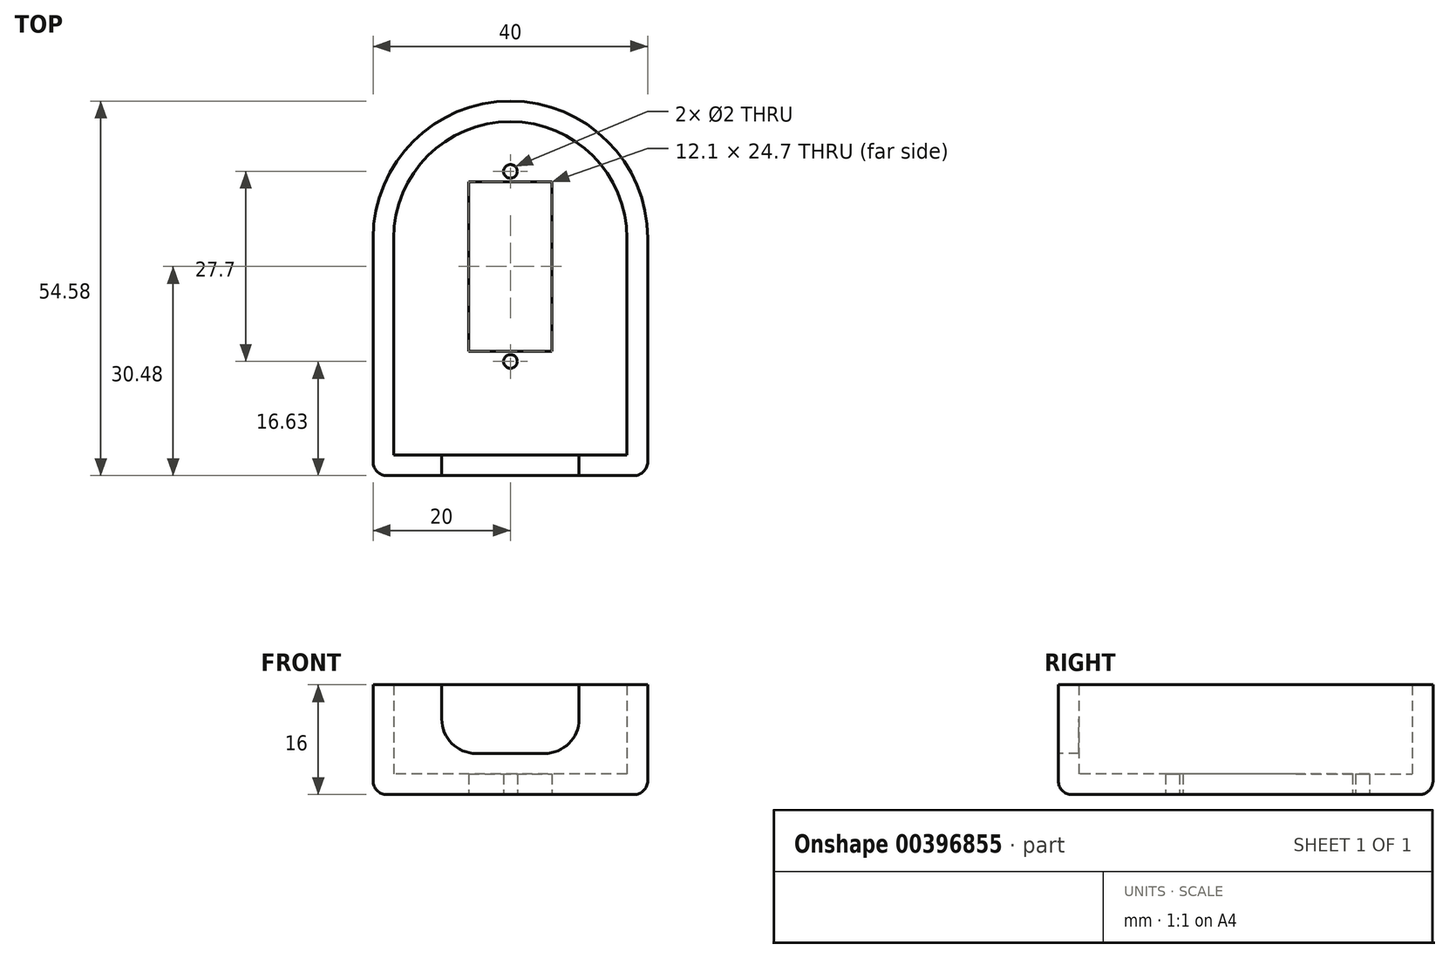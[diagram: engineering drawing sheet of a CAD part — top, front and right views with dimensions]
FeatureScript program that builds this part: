
annotation { "Feature Type Name" : "Feature", "Feature Type Description" : "" }
export const myFeature = defineFeature(function(context is Context, id is Id, definition is map)
    precondition{}
    {
        {
            var Q0;
            Q0=qCreatedBy(makeId("Top.planeOp"),FACE);
            var sketch = newSketch(context, id + "F0", { "sketchPlane" : qUnion([Q0])});
            skLineSegment(sketch, "E0.bottom", {"start": v(0, 22.7) * mm, "end": v(12.1, 22.7) * mm});
            skLineSegment(sketch, "E0.top", {"start": v(0, 0) * mm, "end": v(12.1, 0) * mm});
            skLineSegment(sketch, "E0.left", {"start": v(0, 22.7) * mm, "end": v(0, 0) * mm});
            skLineSegment(sketch, "E0.right", {"start": v(12.1, 22.7) * mm, "end": v(12.1, 0) * mm});
            skLineSegment(sketch, "E1.bottom", {"start": v(-3, 27.5) * mm, "end": v(15.1, 27.5) * mm});
            skLineSegment(sketch, "E1.top", {"start": v(-3, -4.8) * mm, "end": v(15.1, -4.8) * mm});
            skLineSegment(sketch, "E1.left", {"start": v(-3, 27.5) * mm, "end": v(-3, -4.8) * mm});
            skLineSegment(sketch, "E1.right", {"start": v(15.1, 27.5) * mm, "end": v(15.1, -4.8) * mm});
            skLineSegment(sketch, "E2", {"start": v(0, 11.35) * mm, "end": v(-3, 11.35) * mm});
            skPoint(sketch, "E2.startSnap0", {"position": v(0, 11.35) * mm});
            skCircle(sketch, "E3", {"center": v(6.05, -2.5) * mm, "radius": 1 * mm});
            skPoint(sketch, "E3.centerSnap0", {"position": v(6.05, 0) * mm});
            skCircle(sketch, "E4", {"center": v(6.05, 25.2) * mm, "radius": 1 * mm});
            skPoint(sketch, "E4.centerSnap0", {"position": v(6.05, 22.7) * mm});
            skLineSegment(sketch, "E5.top", {"start": v(-13.95, -19.13) * mm, "end": v(26.05, -19.13) * mm});
            skLineSegment(sketch, "E5.left", {"start": v(-13.95, 15.45) * mm, "end": v(-13.95, -19.13) * mm});
            skLineSegment(sketch, "E5.right", {"start": v(26.05, 15.45) * mm, "end": v(26.05, -19.13) * mm});
            skLineSegment(sketch, "E6", {"start": v(6.05, -19.13) * mm, "end": v(6.05, 0) * mm});
            skCircle(sketch, "E7", {"center": v(6.05, 15.45) * mm, "radius": 20 * mm});
            skCircle(sketch, "E8", {"center": v(6.05, 15.45) * mm, "radius": 17 * mm});
            skLineSegment(sketch, "E9", {"start": v(-10.95, 15.45) * mm, "end": v(-10.95, -16.13) * mm});
            skLineSegment(sketch, "E10", {"start": v(-10.95, -16.13) * mm, "end": v(23.05, -16.13) * mm});
            skLineSegment(sketch, "E11", {"start": v(23.05, -16.13) * mm, "end": v(23.05, 15.45) * mm});
            skLineSegment(sketch, "E12.bottom", {"start": v(0, -1) * mm, "end": v(12.1, -1) * mm});
            skLineSegment(sketch, "E12.top", {"start": v(0, 23.7) * mm, "end": v(12.1, 23.7) * mm});
            skLineSegment(sketch, "E12.left", {"start": v(0, -1) * mm, "end": v(0, 23.7) * mm});
            skLineSegment(sketch, "E12.right", {"start": v(12.1, -1) * mm, "end": v(12.1, 23.7) * mm});
            skSolve(sketch);
        }
        {
            var Q0;
            Q0 = qSketchRegion(id + "F0", true);
            var Q1;
            {var subQ3=sQuery(id+"F0.wireOp",EDGE,"E2");Q1=makeQuery(id+"F0.imprint","IMPRINT",FACE,{"disambiguationData":[TD([[makeQuery(id+"F0.imprint","IMPRINT",EDGE,{"derivedFrom":subQ3}),1.0]])]});}
            var Q2;
            {var subQ0=sQuery(id+"F0.wireOp",EDGE,"E10");var subQ1=sQuery(id+"F0.wireOp",EDGE,"E6");var subQ2=makeQuery(id+"F0.imprint","INTERSECT",VERTEX,{"derivedFrom":[subQ1,subQ0]});Q2=makeQuery(id+"F0.imprint","IMPRINT",FACE,{"disambiguationData":[TD([[makeQuery(id+"F0.imprint","IMPRINT",EDGE,{"disambiguationData":[TD([[subQ2,-1.0]])],"derivedFrom":subQ1}),1.0]])]});}
            var Q3;
            {var subQ0=sQuery(id+"F0.wireOp",EDGE,"E10");var subQ1=sQuery(id+"F0.wireOp",EDGE,"E6");var subQ2=makeQuery(id+"F0.imprint","INTERSECT",VERTEX,{"derivedFrom":[subQ1,subQ0]});Q3=makeQuery(id+"F0.imprint","IMPRINT",FACE,{"disambiguationData":[TD([[makeQuery(id+"F0.imprint","IMPRINT",EDGE,{"disambiguationData":[TD([[subQ2,-1.0]])],"derivedFrom":subQ1}),-1.0]])]});}
            var Q4;
            {var subQ1=sQuery(id+"F0.wireOp",EDGE,"E1.bottom");Q4=makeQuery(id+"F0.imprint","IMPRINT",FACE,{"disambiguationData":[TD([[makeQuery(id+"F0.imprint","IMPRINT",EDGE,{"derivedFrom":subQ1}),1.0]])]});}
            var Q5;
            {var subQ0=sQuery(id+"F0.wireOp",EDGE,"E8");var subQ1=sQuery(id+"F0.wireOp",EDGE,"E1.right");var subQ2=makeQuery(id+"F0.imprint","INTERSECT",VERTEX,{"derivedFrom":[subQ1,subQ0]});Q5=makeQuery(id+"F0.imprint","IMPRINT",FACE,{"disambiguationData":[TD([[makeQuery(id+"F0.imprint","IMPRINT",EDGE,{"disambiguationData":[TD([[subQ2,-1.0]])],"derivedFrom":subQ1}),1.0]])]});}
            var Q6;
            {var subQ0=sQuery(id+"F0.wireOp",EDGE,"E8");var subQ1=sQuery(id+"F0.wireOp",EDGE,"E1.left");var subQ2=makeQuery(id+"F0.imprint","INTERSECT",VERTEX,{"derivedFrom":[subQ1,subQ0]});Q6=makeQuery(id+"F0.imprint","IMPRINT",FACE,{"disambiguationData":[TD([[makeQuery(id+"F0.imprint","IMPRINT",EDGE,{"disambiguationData":[TD([[subQ2,-1.0]])],"derivedFrom":subQ1}),-1.0]])]});}
            var Q7;
            {var subQ5=sQuery(id+"F0.wireOp",EDGE,"E8");var subQ7=sQuery(id+"F0.wireOp",EDGE,"E1.left");var subQ9=makeQuery(id+"F0.imprint","INTERSECT",VERTEX,{"derivedFrom":[subQ7,subQ5]});Q7=makeQuery(id+"F0.imprint","IMPRINT",FACE,{"disambiguationData":[TD([[makeQuery(id+"F0.imprint","IMPRINT",EDGE,{"disambiguationData":[TD([[subQ9,-1.0]])],"derivedFrom":subQ7}),1.0]])]});}
            var Q8;
            {var subQ0=sQuery(id+"F0.wireOp",EDGE,"E1.left");var subQ1=sQuery(id+"F0.wireOp",EDGE,"E1.top");var subQ2=makeQuery(id+"F0.imprint","INTERSECT",VERTEX,{"derivedFrom":[subQ1,subQ0]});Q8=makeQuery(id+"F0.imprint","IMPRINT",FACE,{"disambiguationData":[TD([[makeQuery(id+"F0.imprint","IMPRINT",EDGE,{"disambiguationData":[TD([[subQ2,-1.0]])],"derivedFrom":subQ1}),1.0]])]});}
            var Q9;
            {var subQ0=sQuery(id+"F0.wireOp",EDGE,"E1.right");var subQ1=sQuery(id+"F0.wireOp",EDGE,"E1.top");var subQ2=makeQuery(id+"F0.imprint","INTERSECT",VERTEX,{"derivedFrom":[subQ1,subQ0]});Q9=makeQuery(id+"F0.imprint","IMPRINT",FACE,{"disambiguationData":[TD([[makeQuery(id+"F0.imprint","IMPRINT",EDGE,{"disambiguationData":[TD([[subQ2,1.0]])],"derivedFrom":subQ1}),1.0]])]});}
            var Q10;
            {var subQ1=sQuery(id+"F0.wireOp",EDGE,"E1.right");var subQ5=sQuery(id+"F0.wireOp",EDGE,"E8");var subQ9=makeQuery(id+"F0.imprint","INTERSECT",VERTEX,{"derivedFrom":[subQ1,subQ5]});Q10=makeQuery(id+"F0.imprint","IMPRINT",FACE,{"disambiguationData":[TD([[makeQuery(id+"F0.imprint","IMPRINT",EDGE,{"disambiguationData":[TD([[subQ9,-1.0]])],"derivedFrom":subQ1}),-1.0]])]});}
            var Q11;
            {var subQ0=sQuery(id+"F0.wireOp",EDGE,"E6");var subQ1=sQuery(id+"F0.wireOp",EDGE,"E3");var subQ2=makeQuery(id+"F0.imprint","INTERSECT",VERTEX,{"disambiguationData":[OD(0.0)],"derivedFrom":[subQ1,subQ0]});Q11=makeQuery(id+"F0.imprint","IMPRINT",FACE,{"disambiguationData":[TD([[makeQuery(id+"F0.imprint","IMPRINT",EDGE,{"disambiguationData":[TD([[subQ2,1.0]])],"derivedFrom":subQ1}),-1.0]])]});}
            var Q12;
            {var subQ0=sQuery(id+"F0.wireOp",EDGE,"E6");var subQ1=sQuery(id+"F0.wireOp",EDGE,"E3");var subQ2=makeQuery(id+"F0.imprint","INTERSECT",VERTEX,{"disambiguationData":[OD(0.0)],"derivedFrom":[subQ1,subQ0]});Q12=makeQuery(id+"F0.imprint","IMPRINT",FACE,{"disambiguationData":[TD([[makeQuery(id+"F0.imprint","IMPRINT",EDGE,{"disambiguationData":[TD([[subQ2,-1.0]])],"derivedFrom":subQ1}),-1.0]])]});}
            var Q13;
            {var subQ11=sQuery(id+"F0.wireOp",EDGE,"E1.bottom");Q13=makeQuery(id+"F0.imprint","IMPRINT",FACE,{"disambiguationData":[TD([[makeQuery(id+"F0.imprint","IMPRINT",EDGE,{"derivedFrom":subQ11}),-1.0]])]});}
            extrude(context, id + "F1", {"entities" : qUnion([Q0, Q1, Q2, Q3, Q4, Q5, Q6, Q7, Q8, Q9, Q10, Q11, Q12, Q13]), "depth" : 3 * mm});
        }
        {
            var Q0;
            {var subQ1=sQuery(id+"F0.wireOp",EDGE,"E5.left");Q0=makeQuery(id+"F0.imprint","IMPRINT",FACE,{"disambiguationData":[TD([[makeQuery(id+"F0.imprint","IMPRINT",EDGE,{"derivedFrom":subQ1}),1.0]])]});}
            var Q1;
            {var subQ1=sQuery(id+"F0.wireOp",EDGE,"E5.right");Q1=makeQuery(id+"F0.imprint","IMPRINT",FACE,{"disambiguationData":[TD([[makeQuery(id+"F0.imprint","IMPRINT",EDGE,{"derivedFrom":subQ1}),-1.0]])]});}
            var Q2;
            {var subQ0=sQuery(id+"F0.wireOp",EDGE,"E7");var subQ4=makeQuery(id+"F0.imprint","INTERSECT",VERTEX,{"derivedFrom":[sQuery(id+"F0.wireOp",EDGE,"E5.left"),subQ0]});Q2=makeQuery(id+"F0.imprint","IMPRINT",FACE,{"disambiguationData":[TD([[makeQuery(id+"F0.imprint","IMPRINT",EDGE,{"disambiguationData":[TD([[subQ4,1.0]])],"derivedFrom":subQ0}),1.0]])]});}
            extrude(context, id + "F2", {"entities" : qUnion([Q0, Q1, Q2]), "operationType" : NewBodyOperationType.ADD, "depth" : 16 * mm});
        }
        {
            var Q0;
            Q0=makeQuery(id+"F2.opExtrude","CAP_EDGE",EDGE,{"disambiguationData":[OSD([sQuery(id+"FoOm9mcpyAAcKK5_1.wireOp",EDGE,"GcfQukfY-8nN6-G3zW-65xT-WTSIB9kCBruh.right")])],"isStart":true});
            var Q1;
            Q1=makeQuery(id+"F2.opExtrude","CAP_EDGE",EDGE,{"disambiguationData":[OSD([sQuery(id+"FoOm9mcpyAAcKK5_1.wireOp",EDGE,"54IPlG1U-AUWy-TRX5-auCB-k9ajS3RtIQhU.right")])],"isStart":true});
            var Q2;
            Q2=makeQuery(id+"F1.opExtrude","CAP_EDGE",EDGE,{"disambiguationData":[OSD([sQuery(id+"F0.wireOp",EDGE,"E5.right")])],"isStart":true});
            var Q3;
            Q3=makeQuery(id+"F1.opExtrude","CAP_EDGE",EDGE,{"disambiguationData":[OSD([sQuery(id+"F0.wireOp",EDGE,"E5.left")])],"isStart":true});
            var Q4;
            Q4=makeQuery(id+"F1.opExtrude","CAP_EDGE",EDGE,{"disambiguationData":[OSD([sQuery(id+"F0.wireOp",EDGE,"E5.top")])],"isStart":true});
            var Q5;
            {var subQ0=sQuery(id+"F0.wireOp",EDGE,"E5.right");var subQ1=sQuery(id+"F0.wireOp",EDGE,"E5.top");Q5=makeQuery(id+"F2.boolean.opBoolean","MERGE",EDGE,{"derivedFrom":[makeQuery(id+"F1.opExtrude","SWEPT_EDGE",EDGE,{"disambiguationData":[OSD([subQ1,subQ0])]}),makeQuery(id+"F2.opExtrude","SWEPT_EDGE",EDGE,{"disambiguationData":[OSD([subQ1,subQ0])]})]});}
            var Q6;
            {var subQ0=sQuery(id+"F0.wireOp",EDGE,"E5.left");var subQ1=sQuery(id+"F0.wireOp",EDGE,"E5.top");Q6=makeQuery(id+"F2.boolean.opBoolean","MERGE",EDGE,{"derivedFrom":[makeQuery(id+"F1.opExtrude","SWEPT_EDGE",EDGE,{"disambiguationData":[OSD([subQ1,subQ0])]}),makeQuery(id+"F2.opExtrude","SWEPT_EDGE",EDGE,{"disambiguationData":[OSD([subQ1,subQ0])]})]});}
            fillet(context, id + "F3", {"entities" : qUnion([Q0, Q1, Q2, Q3, Q4, Q5, Q6]), "radius" : 2 * mm, "tangentPropagation" : true, "allowEdgeOverflow" : false});
        }
        {
            var Q0;
            {var subQ0=sQuery(id+"F0.wireOp",EDGE,"E5.top");Q0=makeQuery(id+"F2.boolean.opBoolean","MERGE",FACE,{"derivedFrom":[makeQuery(id+"F1.opExtrude","SWEPT_FACE",FACE,{"disambiguationData":[OSD([subQ0])]}),makeQuery(id+"F2.opExtrude","SWEPT_FACE",FACE,{"disambiguationData":[OSD([subQ0])]})]});}
            var sketch = newSketch(context, id + "F4", { "sketchPlane" : qUnion([Q0])});
            skLineSegment(sketch, "E13.bottom", {"start": v(-3.95, 16) * mm, "end": v(16.05, 16) * mm});
            skLineSegment(sketch, "E13.top", {"start": v(-3.95, 6) * mm, "end": v(16.05, 6) * mm});
            skLineSegment(sketch, "E13.left", {"start": v(-3.95, 16) * mm, "end": v(-3.95, 6) * mm});
            skLineSegment(sketch, "E13.right", {"start": v(16.05, 16) * mm, "end": v(16.05, 6) * mm});
            skLineSegment(sketch, "E14", {"start": v(6.05, 16) * mm, "end": v(6.05, 6) * mm});
            skSolve(sketch);
        }
        {
            var Q0;
            Q0 = qSketchRegion(id + "F4", true);
            var Q1;
            Q1=makeQuery(id+"F2.opExtrude","SWEPT_FACE",FACE,{"disambiguationData":[OSD([sQuery(id+"F0.wireOp",EDGE,"E10")])]});
            extrude(context, id + "F5", {"entities" : qUnion([Q0]), "operationType" : NewBodyOperationType.REMOVE, "endBound" : BoundingType.UP_TO_SURFACE, "oppositeDirection" : true, "endBoundEntityFace" : qUnion([Q1]), "depth" : 25 * mm});
        }
        {
            var Q0;
            Q0=makeQuery(id+"F5.boolean.opBoolean","COPY",EDGE,{"derivedFrom":makeQuery(id+"F5.opExtrude","SWEPT_EDGE",EDGE,{"disambiguationData":[OSD([sQuery(id+"F4.wireOp",EDGE,"E13.top"),sQuery(id+"F4.wireOp",EDGE,"E13.left")])]})});
            var Q1;
            Q1=makeQuery(id+"F5.boolean.opBoolean","COPY",EDGE,{"derivedFrom":makeQuery(id+"F5.opExtrude","SWEPT_EDGE",EDGE,{"disambiguationData":[OSD([sQuery(id+"F4.wireOp",EDGE,"E13.top"),sQuery(id+"F4.wireOp",EDGE,"E13.right")])]})});
            fillet(context, id + "F6", {"entities" : qUnion([Q0, Q1]), "radius" : 5 * mm, "tangentPropagation" : true, "allowEdgeOverflow" : false});
        }
    });
